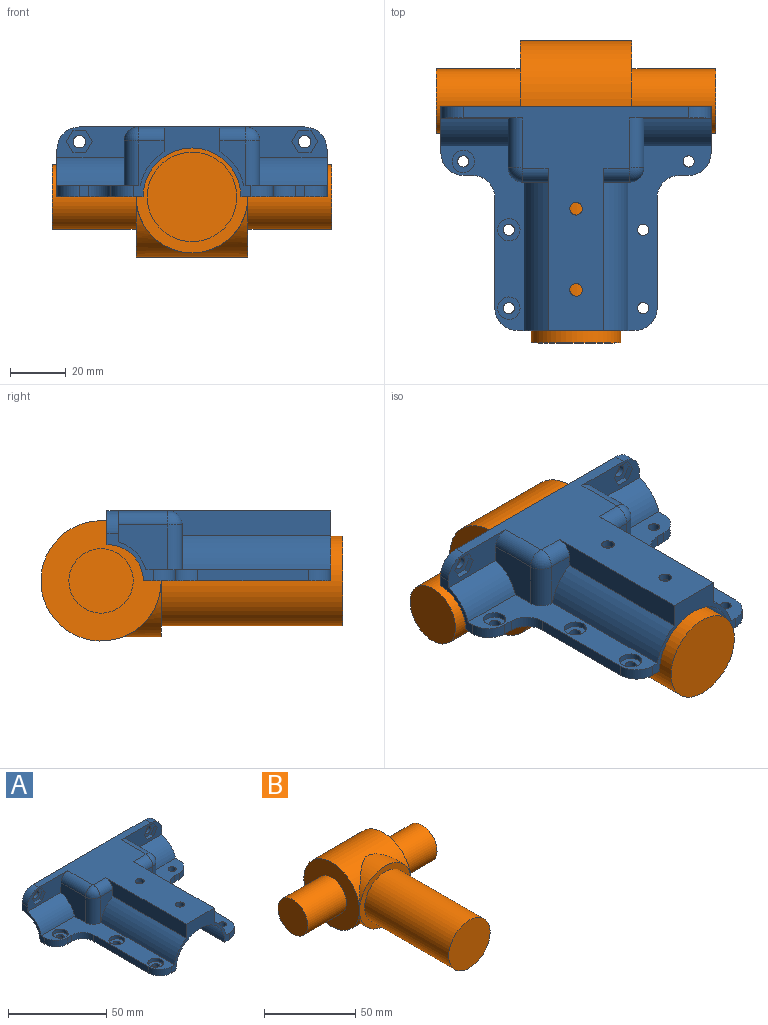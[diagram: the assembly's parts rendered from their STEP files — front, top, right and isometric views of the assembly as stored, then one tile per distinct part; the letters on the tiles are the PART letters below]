
ASSEMBLY  parts=2 mates=1
PART A: 89 faces, bbox 96.6x79.9x25 mm
  f0: plane 29x11.06mm, normal (0,-1,0), area 201.7mm2, adj f1,f2,f3,f27,f30,f73,f76,f77
  f1: plane 17.67x16mm, normal (1,0,0), area 216mm2, adj f0,f2,f3,f25,f55
  f2: cylinder r=14.5mm len=24mm, axis (1,0,0), area 352.1mm2, adj f0,f1,f30,f55
  f3: cylinder r=5mm len=17.67mm, axis (0,-1,0), area 138.7mm2, adj f0,f1,f27,f41
  f4: plane 17.67x16mm, normal (-1,0,0), area 216mm2, adj f5,f6,f7,f23,f70
  f5: cylinder r=14.5mm len=24mm, axis (1,0,0), area 352.1mm2, adj f4,f7,f33,f70
  f6: cylinder r=5mm len=17.67mm, axis (0,1,0), area 138.7mm2, adj f4,f27,f43,f70
  f7: plane 66.01x29.71mm, normal (0,0,1), area 659.1mm2, adj f4,f5,f18,f19,f20,f23,f33,f50
  f8: cylinder r=2mm len=4mm, axis (0,0,-1), area 25.1mm2, adj f16,f68
  f9: cylinder r=2mm len=4mm, axis (0,0,-1), area 25.1mm2, adj f16,f66
  f10: cylinder r=2mm len=4mm, axis (0,0,-1), area 25.1mm2, adj f16,f64
  f11: plane 21.67x18.5mm, normal (-1,0,0), area 268.1mm2, adj f14,f17,f26,f31,f35
  f12: plane 21.67x18.5mm, normal (1,0,0), area 268.1mm2, adj f15,f16,f26,f32,f39
  f13: plane 38x18.5mm, normal (0,1,0), area 221.9mm2, adj f14,f15,f16,f17,f22,f37
  f14: cylinder r=3.78mm len=18.5mm, axis (0,0,-1), area 109.8mm2, adj f11,f13,f17,f36
  f15: cylinder r=3.78mm len=18.5mm, axis (0,0,-1), area 109.8mm2, adj f12,f13,f16,f38
  f16: plane 66.95x30.78mm, normal (0,0,-1), area 877.5mm2, adj f8,f9,f10,f12,f13,f15,f18,f22
  f17: plane 66.95x30.78mm, normal (0,0,-1), area 877.5mm2, adj f11,f13,f14,f18,f22,f30,f31,f56
  f18: plane 42x25mm, normal (0,-1,0), area 241.5mm2, adj f7,f16,f17,f19,f21,f22,f27,f28
  f19: cylinder r=19mm len=53mm, axis (0,-1,0), area 810.1mm2, adj f7,f18,f20,f29
  f20: plane 16x9mm, normal (0,-1,0), area 76.7mm2, adj f7,f19,f23,f29,f42
  f21: cylinder r=19mm len=53mm, axis (0,-1,0), area 810.1mm2, adj f18,f24,f28,f55
  f22: cylinder r=17.5mm len=54.5mm, axis (0,-1,0), area 2895mm2, adj f13,f16,f17,f18,f47,f49
  f23: cylinder r=5.28mm len=16mm, axis (0,0,-1), area 132.7mm2, adj f4,f7,f20,f43
  f24: plane 16x9mm, normal (0,-1,0), area 76.7mm2, adj f21,f25,f28,f40,f55
  f25: cylinder r=5.28mm len=16mm, axis (0,0,-1), area 132.7mm2, adj f1,f24,f41,f55
  f26: plane 96.56x12mm, normal (0,1,0), area 631.8mm2, adj f11,f12,f27,f30,f31,f32,f33,f34
  f27: plane 80.56x79.95mm, normal (0,0,1), area 2142.3mm2, adj f0,f3,f6,f18,f26,f28,f29,f40
  f28: plane 58x8.84mm, normal (1,0,0), area 474.1mm2, adj f18,f21,f24,f27,f40
  f29: plane 58x8.84mm, normal (-1,0,0), area 474.1mm2, adj f18,f19,f20,f27,f42
  f30: plane 17x16.5mm, normal (1,0,0), area 51.9mm2, adj f0,f2,f17,f26,f31,f55,f60,f73
  f31: cylinder r=13mm len=25.5mm, axis (1,0,0), area 520.7mm2, adj f11,f17,f26,f30
  f32: cylinder r=13mm len=25.5mm, axis (1,0,0), area 520.7mm2, adj f12,f16,f26,f33
  f33: plane 17x16.5mm, normal (-1,0,0), area 51.9mm2, adj f5,f7,f16,f26,f32,f50,f70,f71
  f34: plane 35.56x20.45mm, normal (0,0,-1), area 727mm2, adj f26,f35,f37,f39
  f35: cylinder r=5mm len=21.67mm, axis (0,1,0), area 166.7mm2, adj f11,f26,f34,f36
  f36: bspline ~6.13x5mm, area 30.4mm2, adj f14,f35,f37
  f37: cylinder r=5mm len=38mm, axis (1,0,0), area 291.5mm2, adj f13,f34,f36,f38
  f38: bspline ~6.13x5mm, area 30.4mm2, adj f15,f37,f39
  f39: cylinder r=5mm len=21.67mm, axis (0,-1,0), area 166.7mm2, adj f12,f26,f34,f38
  f40: cylinder r=5mm len=9mm, axis (-1,0,0), area 70.7mm2, adj f24,f27,f28,f41
  f41: torus R=0.28mm, axis (0,0,1), area 42.7mm2, adj f3,f25,f27,f40
  f42: cylinder r=5mm len=9mm, axis (-1,0,0), area 70.7mm2, adj f20,f27,f29,f43
  f43: torus R=0.28mm, axis (0,0,1), area 42.7mm2, adj f6,f23,f27,f42
  f44: cylinder r=2.25mm len=4.5mm, axis (0,0,1), area 35.3mm2, adj f27,f48
  f45: cylinder r=2.25mm len=4.5mm, axis (0,0,1), area 35.3mm2, adj f27,f46
  f46: plane 8x8mm, normal (0,0,-1), area 34.4mm2, adj f45,f47
  f47: cylinder r=4mm len=8mm, axis (0,0,1), area 131.5mm2, adj f22,f46
  f48: plane 8x8mm, normal (0,0,-1), area 34.4mm2, adj f44,f49
  f49: cylinder r=4mm len=8mm, axis (0,0,1), area 131.5mm2, adj f22,f48
  f50: cylinder r=8mm len=8mm, axis (0,0,-1), area 50.3mm2, adj f7,f16,f33,f51
  f51: plane 4x3.28mm, normal (0,-1,0), area 13.1mm2, adj f7,f16,f50,f52
  f52: cylinder r=8mm len=8mm, axis (0,0,-1), area 50.3mm2, adj f7,f16,f51,f53
  f53: plane 39.45x4mm, normal (-1,0,0), area 157.8mm2, adj f7,f16,f52,f54
  f54: cylinder r=8mm len=8mm, axis (0,0,-1), area 50.3mm2, adj f7,f16,f18,f53
  f55: plane 66.01x29.71mm, normal (0,0,1), area 772.2mm2, adj f1,f2,f18,f21,f24,f25,f30,f56
  f56: cylinder r=8mm len=8mm, axis (0,0,-1), area 50.3mm2, adj f17,f18,f55,f57
  f57: plane 39.45x4mm, normal (1,0,0), area 157.8mm2, adj f17,f55,f56,f58
  f58: cylinder r=8mm len=8mm, axis (0,0,-1), area 50.3mm2, adj f17,f55,f57,f59
  f59: plane 4x3.28mm, normal (0,-1,0), area 13.1mm2, adj f17,f55,f58,f60
  f60: cylinder r=8mm len=8mm, axis (0,0,-1), area 50.3mm2, adj f17,f30,f55,f59
  f61: cylinder r=2mm len=4mm, axis (0,0,-1), area 50.3mm2, adj f17,f55
  f62: cylinder r=2mm len=4mm, axis (0,0,-1), area 50.3mm2, adj f17,f55
  f63: cylinder r=2mm len=4mm, axis (0,0,-1), area 50.3mm2, adj f17,f55
  f64: plane 8x8mm, normal (0,0,1), area 37.7mm2, adj f10,f65
  f65: cylinder r=4mm len=8mm, axis (0,0,-1), area 50.3mm2, adj f7,f64
  f66: plane 8x8mm, normal (0,0,1), area 37.7mm2, adj f9,f67
  f67: cylinder r=4mm len=8mm, axis (0,0,-1), area 50.3mm2, adj f7,f66
  f68: plane 8x8mm, normal (0,0,1), area 37.7mm2, adj f8,f69
  f69: cylinder r=4mm len=8mm, axis (0,0,-1), area 50.3mm2, adj f7,f68
  f70: plane 29x11.06mm, normal (0,-1,0), area 201.7mm2, adj f4,f5,f6,f27,f33,f71,f83,f84
  f71: cylinder r=8mm len=8mm, axis (0,1,0), area 50.3mm2, adj f26,f27,f33,f70
  f72: cylinder r=2.25mm len=4.5mm, axis (0,1,0), area 28.3mm2, adj f26,f82
  f73: cylinder r=8mm len=8mm, axis (0,1,0), area 50.3mm2, adj f0,f26,f27,f30
  f74: cylinder r=2.25mm len=4.5mm, axis (0,1,0), area 28.3mm2, adj f26,f75
  f75: plane 9.24x8mm, normal (0,-1,0), area 39.5mm2, adj f74,f76,f77,f78,f79,f80,f81
  f76: plane 4.62x2mm, normal (0,0,1), area 9.2mm2, adj f0,f75,f77,f79
  f77: plane 4x2.31mm, normal (0.87,0,0.5), area 9.2mm2, adj f0,f75,f76,f78
  f78: plane 4x2.31mm, normal (0.87,0,-0.5), area 9.2mm2, adj f0,f75,f77,f80
  f79: plane 4x2.31mm, normal (-0.87,0,0.5), area 9.2mm2, adj f0,f75,f76,f81
  f80: plane 4.62x2mm, normal (0,0,-1), area 9.2mm2, adj f0,f75,f78,f81
  f81: plane 4x2.31mm, normal (-0.87,0,-0.5), area 9.2mm2, adj f0,f75,f79,f80
  f82: plane 9.24x8mm, normal (0,-1,0), area 39.5mm2, adj f72,f83,f84,f85,f86,f87,f88
  f83: plane 4.62x2mm, normal (0,0,-1), area 9.2mm2, adj f70,f82,f84,f87
  f84: plane 4x2.31mm, normal (-0.87,0,-0.5), area 9.2mm2, adj f70,f82,f83,f85
  f85: plane 4x2.31mm, normal (-0.87,0,0.5), area 9.2mm2, adj f70,f82,f84,f86
  f86: plane 4.62x2mm, normal (0,0,1), area 9.2mm2, adj f70,f82,f85,f88
  f87: plane 4x2.31mm, normal (0.87,0,-0.5), area 9.2mm2, adj f70,f82,f83,f88
  f88: plane 4x2.31mm, normal (0.87,0,0.5), area 9.2mm2, adj f70,f82,f86,f87
PART B: 12 faces, bbox 100x108x43 mm
  f0: cylinder r=20mm len=40mm, axis (0,1,0), area 377.4mm2, adj f2,f5
  f1: cylinder r=20mm len=40mm, axis (0,1,0), area 377.4mm2, adj f2,f5
  f2: plane 40x40mm, normal (0,-1,0), area 452.4mm2, adj f0,f1,f3
  f3: cylinder r=16mm len=65mm, axis (0,1,0), area 6534.5mm2, adj f2,f4
  f4: plane 32x32mm, normal (0,-1,0), area 804.2mm2, adj f3
  f5: cylinder r=21.5mm len=43mm, axis (-1,0,0), area 3917.5mm2, adj f0,f1,f7,f8
  f6: cylinder r=11.5mm len=30mm, axis (-1,0,0), area 2167.7mm2, adj f7,f11
  f7: plane 43x43mm, normal (-1,0,0), area 1036.7mm2, adj f5,f6
  f8: plane 43x43mm, normal (1,0,0), area 1036.7mm2, adj f5,f9
  f9: cylinder r=11.5mm len=30mm, axis (-1,0,0), area 2167.7mm2, adj f8,f10
  f10: plane 23x23mm, normal (1,0,0), area 415.5mm2, adj f9
  f11: plane 23x23mm, normal (-1,0,0), area 415.5mm2, adj f6
PLACE A t=(-26.56,-3.75,1.55)mm
PLACE B t=(-26.56,-6.56,1.55)mm fixed
MATE slider B.f0 <-> A.f19  axis (0,-1,0) through (-26.56,-98.61,1.55)mm
